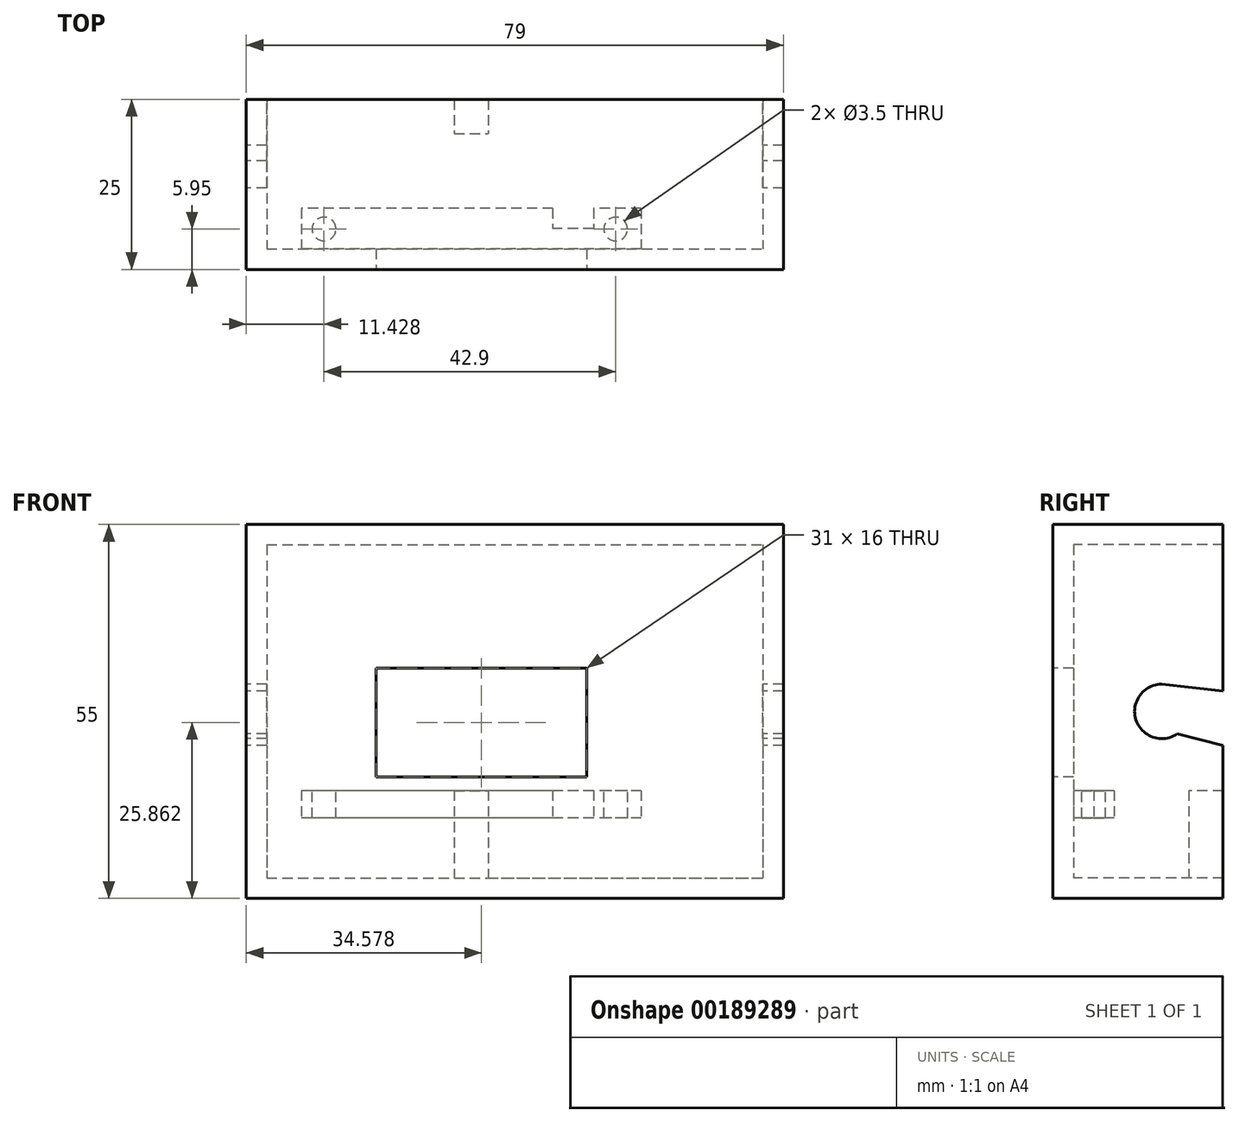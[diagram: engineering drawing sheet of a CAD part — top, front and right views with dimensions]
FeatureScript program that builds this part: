
annotation { "Feature Type Name" : "Feature", "Feature Type Description" : "" }
export const myFeature = defineFeature(function(context is Context, id is Id, definition is map)
    precondition{}
    {
        {
            var Q0;
            Q0=qCreatedBy(makeId("Front.planeOp"),FACE);
            var sketch = newSketch(context, id + "F0", { "sketchPlane" : qUnion([Q0])});
            skLineSegment(sketch, "E0.bottom", {"start": v(39.5, 27.5) * mm, "end": v(-39.5, 27.5) * mm});
            skLineSegment(sketch, "E0.top", {"start": v(39.5, -27.5) * mm, "end": v(-39.5, -27.5) * mm});
            skLineSegment(sketch, "E0.left", {"start": v(39.5, 27.5) * mm, "end": v(39.5, -27.5) * mm});
            skLineSegment(sketch, "E0.right", {"start": v(-39.5, 27.5) * mm, "end": v(-39.5, -27.5) * mm});
            skPoint(sketch, "E0.middle", {"position": v(0, 0) * mm});
            skLineSegment(sketch, "E1.bottom", {"start": v(-36.5, 24.5) * mm, "end": v(36.5, 24.5) * mm});
            skLineSegment(sketch, "E1.top", {"start": v(-36.5, -24.5) * mm, "end": v(36.5, -24.5) * mm});
            skLineSegment(sketch, "E1.left", {"start": v(-36.5, 24.5) * mm, "end": v(-36.5, -24.5) * mm});
            skLineSegment(sketch, "E1.right", {"start": v(36.5, 24.5) * mm, "end": v(36.5, -24.5) * mm});
            skLineSegment(sketch, "E2.bottom", {"start": v(-20.42, 6.36) * mm, "end": v(10.58, 6.36) * mm});
            skLineSegment(sketch, "E2.top", {"start": v(-20.42, -9.64) * mm, "end": v(10.58, -9.64) * mm});
            skLineSegment(sketch, "E2.left", {"start": v(-20.42, 6.36) * mm, "end": v(-20.42, -9.64) * mm});
            skLineSegment(sketch, "E2.right", {"start": v(10.58, 6.36) * mm, "end": v(10.58, -9.64) * mm});
            skLineSegment(sketch, "E3", {"start": v(-35.42, -9.64) * mm, "end": v(17.58, -9.64) * mm, "construction": true});
            skPoint(sketch, "E4", {"position": v(-6.42, -9.64) * mm});
            skSolve(sketch);
        }
        {
            var Q0;
            Q0=makeQuery(id+"F0.imprint","IMPRINT",FACE,{"disambiguationData":[TD([[makeQuery(id+"F0.imprint","IMPRINT",EDGE,{"derivedFrom":sQuery(id+"F0.wireOp",EDGE,"E0.bottom")}),1.0]])]});
            extrude(context, id + "F1", {"entities" : qUnion([Q0]), "oppositeDirection" : true, "depth" : 25 * mm});
        }
        {
            var Q0;
            Q0=makeQuery(id+"F1.opExtrude","SWEPT_FACE",FACE,{"disambiguationData":[OSD([sQuery(id+"F0.wireOp",EDGE,"E0.right")])]});
            var sketch = newSketch(context, id + "F2", { "sketchPlane" : qUnion([Q0])});
            skArc(sketch, "E5", {"start": v(-18.27, -3.3) * mm, "mid": v(-12.07, -0.76) * mm, "end": v(-16.88, 3.9) * mm});
            skPoint(sketch, "E6", {"position": v(-16, 4) * mm});
            skPoint(sketch, "E7", {"position": v(-18.27, -3.3) * mm});
            skLineSegment(sketch, "E8", {"start": v(-16, 4) * mm, "end": v(-25, 3) * mm});
            skLineSegment(sketch, "E9", {"start": v(-18.27, -3.3) * mm, "end": v(-25, -5) * mm});
            skSolve(sketch);
        }
        {
            var Q0;
            {var subQ0=sQuery(id+"F2.wireOp",EDGE,"E9");Q0=makeQuery(id+"F2.imprint","IMPRINT",FACE,{"disambiguationData":[TD([[makeQuery(id+"F2.imprint","IMPRINT",EDGE,{"derivedFrom":subQ0}),-1.0]])]});}
            var Q1;
            Q1=makeQuery(id+"F1.opExtrude","SWEPT_FACE",FACE,{"disambiguationData":[OSD([sQuery(id+"F0.wireOp",EDGE,"E0.left")])]});
            extrude(context, id + "F3", {"entities" : qUnion([Q0]), "operationType" : NewBodyOperationType.REMOVE, "endBound" : BoundingType.UP_TO_SURFACE, "oppositeDirection" : true, "endBoundEntityFace" : qUnion([Q1]), "depth" : 23 * mm});
        }
        {
            var Q0;
            Q0=makeQuery(id+"F0.imprint","IMPRINT",FACE,{"disambiguationData":[TD([[makeQuery(id+"F0.imprint","IMPRINT",EDGE,{"derivedFrom":sQuery(id+"F0.wireOp",EDGE,"E1.bottom")}),-1.0]])]});
            extrude(context, id + "F4", {"entities" : qUnion([Q0]), "operationType" : NewBodyOperationType.ADD, "oppositeDirection" : true, "depth" : 3 * mm});
        }
        {
            var Q0;
            Q0=makeQuery(id+"F4.opExtrude","CAP_FACE",FACE,{"disambiguationData":[OSD([sQuery(id+"F0.wireOp",EDGE,"E1.bottom"),sQuery(id+"F0.wireOp",EDGE,"E1.top"),sQuery(id+"F0.wireOp",EDGE,"E1.left"),sQuery(id+"F0.wireOp",EDGE,"E1.right"),sQuery(id+"F0.wireOp",EDGE,"E2.bottom"),sQuery(id+"F0.wireOp",EDGE,"E2.top"),sQuery(id+"F0.wireOp",EDGE,"E2.left"),sQuery(id+"F0.wireOp",EDGE,"E2.right")])],"isStart":false});
            var sketch = newSketch(context, id + "F5", { "sketchPlane" : qUnion([Q0])});
            skLineSegment(sketch, "E10.bottom", {"start": v(-18.58, -11.64) * mm, "end": v(31.42, -11.64) * mm});
            skLineSegment(sketch, "E10.top", {"start": v(-18.58, -15.64) * mm, "end": v(31.42, -15.64) * mm});
            skLineSegment(sketch, "E10.left", {"start": v(-18.58, -11.64) * mm, "end": v(-18.58, -15.64) * mm});
            skLineSegment(sketch, "E10.right", {"start": v(31.42, -11.64) * mm, "end": v(31.42, -15.64) * mm});
            skLineSegment(sketch, "E11", {"start": v(-11.58, -11.64) * mm, "end": v(-11.58, -15.64) * mm});
            skLineSegment(sketch, "E12", {"start": v(-5.58, -11.64) * mm, "end": v(-5.58, -15.64) * mm});
            skSolve(sketch);
        }
        {
            var Q0;
            {var subQ0=sQuery(id+"F5.wireOp",EDGE,"E11");Q0=makeQuery(id+"F5.imprint","IMPRINT",FACE,{"disambiguationData":[TD([[makeQuery(id+"F5.imprint","IMPRINT",EDGE,{"derivedFrom":subQ0}),1.0]])]});}
            extrude(context, id + "F6", {"entities" : qUnion([Q0]), "operationType" : NewBodyOperationType.ADD, "depth" : 3 * mm});
        }
        {
            var Q0;
            {var subQ0=sQuery(id+"F5.wireOp",EDGE,"E10.right");Q0=makeQuery(id+"F5.imprint","IMPRINT",FACE,{"disambiguationData":[TD([[makeQuery(id+"F5.imprint","IMPRINT",EDGE,{"derivedFrom":subQ0}),-1.0]])]});}
            var Q1;
            {var subQ0=sQuery(id+"F5.wireOp",EDGE,"E10.left");Q1=makeQuery(id+"F5.imprint","IMPRINT",FACE,{"disambiguationData":[TD([[makeQuery(id+"F5.imprint","IMPRINT",EDGE,{"derivedFrom":subQ0}),1.0]])]});}
            extrude(context, id + "F7", {"entities" : qUnion([Q0, Q1]), "operationType" : NewBodyOperationType.ADD, "depth" : 6 * mm});
        }
        {
            var Q0;
            Q0=makeQuery(id+"F1.opExtrude","SWEPT_FACE",FACE,{"disambiguationData":[OSD([sQuery(id+"F0.wireOp",EDGE,"E1.top")])]});
            var sketch = newSketch(context, id + "F8", { "sketchPlane" : qUnion([Q0])});
            skLineSegment(sketch, "E13.bottom", {"start": v(-8.92, 25) * mm, "end": v(-3.92, 25) * mm});
            skLineSegment(sketch, "E13.top", {"start": v(-8.92, 20) * mm, "end": v(-3.92, 20) * mm});
            skLineSegment(sketch, "E13.left", {"start": v(-8.92, 25) * mm, "end": v(-8.92, 20) * mm});
            skLineSegment(sketch, "E13.right", {"start": v(-3.92, 25) * mm, "end": v(-3.92, 20) * mm});
            skPoint(sketch, "E14", {"position": v(-6.42, 20) * mm});
            skSolve(sketch);
        }
        {
            var Q0;
            Q0=makeQuery(id+"F8.imprint","IMPRINT",FACE,{"disambiguationData":[TD([[makeQuery(id+"F8.imprint","IMPRINT",EDGE,{"derivedFrom":sQuery(id+"F8.wireOp",EDGE,"E13.bottom")}),-1.0]])]});
            extrude(context, id + "F9", {"entities" : qUnion([Q0]), "operationType" : NewBodyOperationType.ADD, "depth" : 12.86 * mm});
        }
        {
            var Q0;
            {var subQ0=sQuery(id+"F5.wireOp",EDGE,"E10.bottom");Q0=makeQuery(id+"F7.boolean.opBoolean","MERGE",FACE,{"derivedFrom":[makeQuery(id+"F6.opExtrude","SWEPT_FACE",FACE,{"disambiguationData":[OSD([subQ0])]}),makeQuery(id+"F7.opExtrude","SWEPT_FACE",FACE,{"disambiguationData":[OSD([subQ0]),TDD([makeQuery(id+"F5.imprint","IMPRINT",EDGE,{"disambiguationData":[TD([[makeQuery(id+"F5.imprint","INTERSECT",VERTEX,{"derivedFrom":[subQ0,sQuery(id+"F5.wireOp",EDGE,"E10.left")]}),-1.0]])],"derivedFrom":subQ0})])]}),makeQuery(id+"F7.opExtrude","SWEPT_FACE",FACE,{"disambiguationData":[OSD([subQ0]),TDD([makeQuery(id+"F5.imprint","IMPRINT",EDGE,{"disambiguationData":[TD([[makeQuery(id+"F5.imprint","INTERSECT",VERTEX,{"derivedFrom":[subQ0,sQuery(id+"F5.wireOp",EDGE,"E10.right")]}),1.0]])],"derivedFrom":subQ0})])]})]});}
            var sketch = newSketch(context, id + "F10", { "sketchPlane" : qUnion([Q0])});
            skCircle(sketch, "E15", {"center": v(14.83, 5.95) * mm, "radius": 1.75 * mm});
            skPoint(sketch, "E16", {"position": v(14.83, 4.2) * mm});
            skPoint(sketch, "E17", {"position": v(16.58, 5.95) * mm});
            skCircle(sketch, "E18", {"center": v(-28.07, 5.95) * mm, "radius": 1.75 * mm});
            skPoint(sketch, "E19", {"position": v(-28.07, 4.2) * mm});
            skPoint(sketch, "E20", {"position": v(-29.82, 5.95) * mm});
            skPoint(sketch, "E21", {"position": v(13.08, 5.95) * mm});
            skPoint(sketch, "E22", {"position": v(-26.32, 5.95) * mm});
            skSolve(sketch);
        }
        {
            var Q0;
            Q0=makeQuery(id+"F10.imprint","IMPRINT",FACE,{"disambiguationData":[TD([[makeQuery(id+"F10.imprint","IMPRINT",EDGE,{"derivedFrom":sQuery(id+"F10.wireOp",EDGE,"E15")}),1.0]])]});
            var Q1;
            Q1=makeQuery(id+"F10.imprint","IMPRINT",FACE,{"disambiguationData":[TD([[makeQuery(id+"F10.imprint","IMPRINT",EDGE,{"derivedFrom":sQuery(id+"F10.wireOp",EDGE,"E18")}),1.0]])]});
            var Q2;
            {var subQ0=sQuery(id+"F5.wireOp",EDGE,"E10.top");Q2=makeQuery(id+"F7.boolean.opBoolean","MERGE",FACE,{"derivedFrom":[makeQuery(id+"F6.opExtrude","SWEPT_FACE",FACE,{"disambiguationData":[OSD([subQ0])]}),makeQuery(id+"F7.opExtrude","SWEPT_FACE",FACE,{"disambiguationData":[OSD([subQ0]),TDD([makeQuery(id+"F5.imprint","IMPRINT",EDGE,{"disambiguationData":[TD([[makeQuery(id+"F5.imprint","INTERSECT",VERTEX,{"derivedFrom":[subQ0,sQuery(id+"F5.wireOp",EDGE,"E10.left")]}),-1.0]])],"derivedFrom":subQ0})])]}),makeQuery(id+"F7.opExtrude","SWEPT_FACE",FACE,{"disambiguationData":[OSD([subQ0]),TDD([makeQuery(id+"F5.imprint","IMPRINT",EDGE,{"disambiguationData":[TD([[makeQuery(id+"F5.imprint","INTERSECT",VERTEX,{"derivedFrom":[subQ0,sQuery(id+"F5.wireOp",EDGE,"E10.right")]}),1.0]])],"derivedFrom":subQ0})])]})]});}
            extrude(context, id + "F11", {"entities" : qUnion([Q0, Q1]), "operationType" : NewBodyOperationType.REMOVE, "endBound" : BoundingType.UP_TO_SURFACE, "oppositeDirection" : true, "endBoundEntityFace" : qUnion([Q2]), "depth" : 25 * mm});
        }
    });
